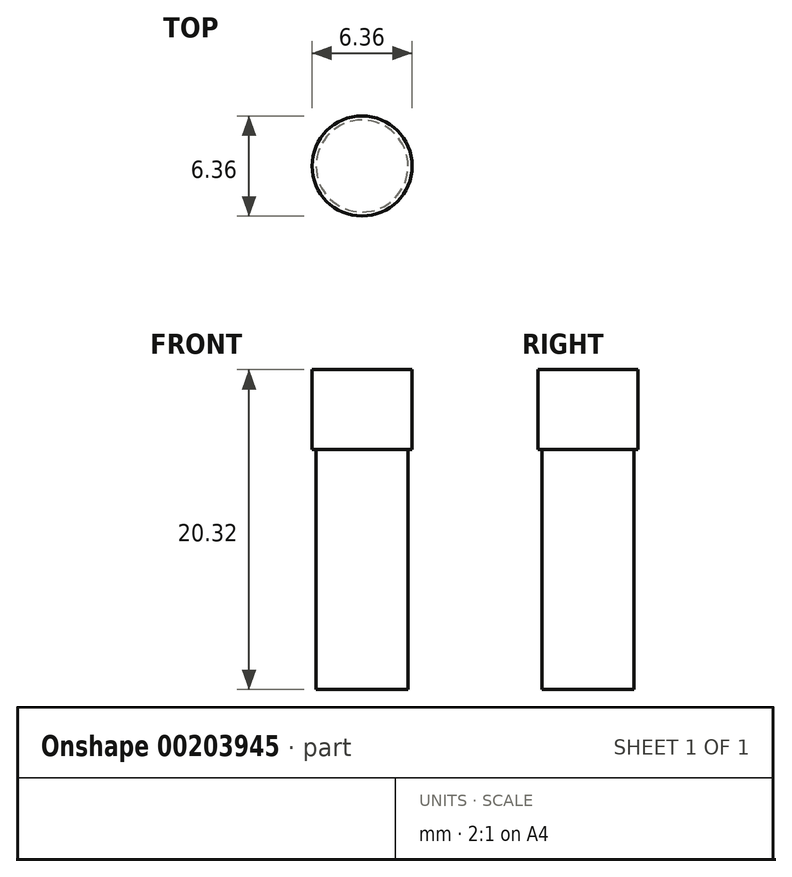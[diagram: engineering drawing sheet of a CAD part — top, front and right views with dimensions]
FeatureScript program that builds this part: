
annotation { "Feature Type Name" : "Feature", "Feature Type Description" : "" }
export const myFeature = defineFeature(function(context is Context, id is Id, definition is map)
    precondition{}
    {
        {
            var Q0;
            Q0=qCreatedBy(makeId("Top.planeOp"),FACE);
            var sketch = newSketch(context, id + "F0", { "sketchPlane" : qUnion([Q0])});
            skCircle(sketch, "E0", {"center": v(0, 0) * mm, "radius": 2.92 * mm});
            skCircle(sketch, "E1", {"center": v(0, 0) * mm, "radius": 3.18 * mm});
            skSolve(sketch);
        }
        {
            var Q0;
            Q0=makeQuery(id+"F0.imprint","IMPRINT",FACE,{"disambiguationData":[TD([[makeQuery(id+"F0.imprint","IMPRINT",EDGE,{"derivedFrom":sQuery(id+"F0.wireOp",EDGE,"E0")}),1.0]])]});
            extrude(context, id + "F1", {"entities" : qUnion([Q0]), "depth" : 15.24 * mm});
        }
        {
            var Q0;
            Q0=makeQuery(id+"F1.opExtrude","CAP_FACE",FACE,{"disambiguationData":[OSD([sQuery(id+"F0.wireOp",EDGE,"E0")])],"isStart":false});
            var sketch = newSketch(context, id + "F2", { "sketchPlane" : qUnion([Q0])});
            skCircle(sketch, "E2", {"center": v(0, 0) * mm, "radius": 3.17 * mm});
            skSolve(sketch);
        }
        {
            var Q0;
            Q0 = qSketchRegion(id + "F2", true);
            extrude(context, id + "F3", {"entities" : qUnion([Q0]), "operationType" : NewBodyOperationType.ADD, "depth" : 5.08 * mm});
        }
    });
